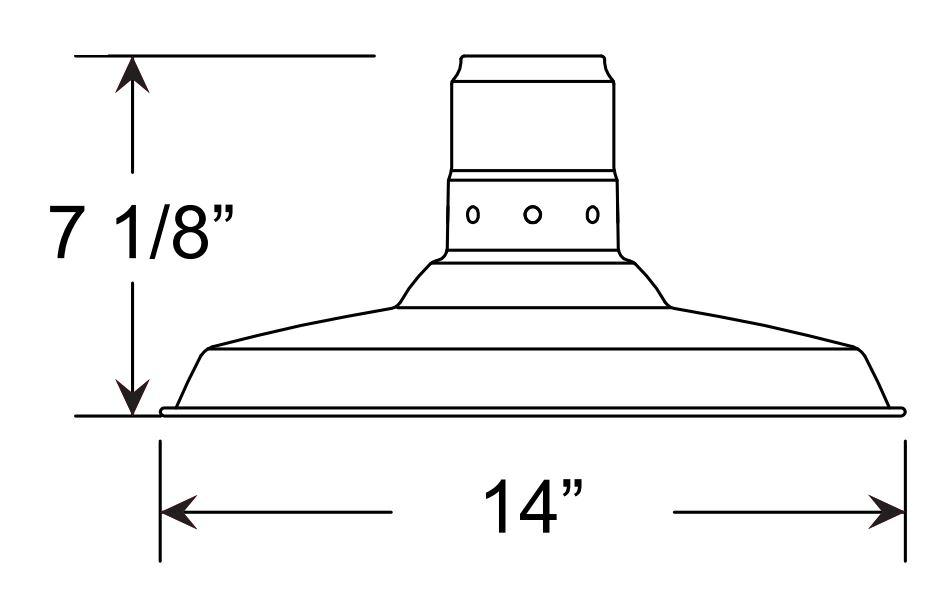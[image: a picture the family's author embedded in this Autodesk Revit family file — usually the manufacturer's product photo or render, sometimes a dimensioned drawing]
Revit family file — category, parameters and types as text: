
# Revit family: Angle_LED
name_source: partatom
category: Lighting Fixtures
units: mm (PartAtom-declared; Revit-internal decimal feet)

## family parameters
Always vertical = Yes
Cut with Voids When Loaded = No
Light Source = Yes
OmniClass Number = 23.80.70.00
OmniClass Title = Lighting
Part Type = Normal
Room Calculation Point = No
Round Connector Dimension = Use Diameter
Shared = No
Work Plane-Based = No

## types (4) — shared parameters
Body Colour = Spun aluminium
Body Material = body
CRI = >90
Canopy Body = body
Color Filter = 16777215
Construction Material = Heavy Duty spun aluminum.
Default Elevation = 0' - 0"
Description = 120-277 Voltage
Dimming = 1%
Dimming Lamp Color Temperature Shift = <None>
Efficiency = 65-125 lumens per watt
Lamp = LED
Life = L70 50,000 hours
Load Classification = Lighting
Manufacturer = ANP Lighting
Power Factor = 1
Tilt Angle = 90.00°
URL = https://www.anplighting.com
Voltage = 120 V
Warranty = 5 year limited warranty

## per-type parameters (varying)
| type | A807 | A810 | A812 | A814 | Apparent Load | Fixture Diameter | Fixture Height | Photometric Web File | Wattage Comments | Weight |
| A807 | Yes | No | No | No | 10 VA | 0' - 7" | 0' - 6 1/2" | A807M009LDNW40K.IES | 10W | 1.0 lb |
| A810 | No | Yes | No | No | 16 VA | 0' - 10" | 0' - 8 1/2" | A810M010LDDW40K.IES | 16W | 1.0 lb |
| A812 | No | No | Yes | No | 24 VA | 1' - 0" | 0' - 10" | A814M024LDDW40K.IES | 24W | 1.0 lb |
| A814 | No | No | No | Yes | 24 VA | 1' - 2 1/2" | 1' - 0" | A814M016LDNW40K.ies | 24 W | 1.5 lb |

note: column(s) folded — value = type name in every type: Model

## geometry (parser evidence)
native form markers: Sweep x37
no freeform markers — native parametric forms only
